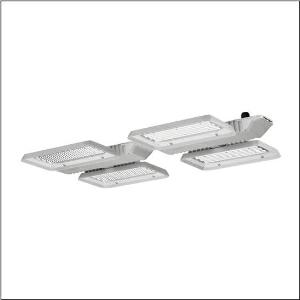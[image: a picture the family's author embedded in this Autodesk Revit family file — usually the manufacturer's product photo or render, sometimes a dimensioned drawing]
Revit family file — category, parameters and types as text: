
# Revit family: highbay_11_51hla2d24nca
name_source: partatom
category: Lighting Fixtures
units: mm (PartAtom-declared; Revit-internal decimal feet)

## family parameters
Cut with Voids When Loaded = No
Host = Face
Light Source = No
Part Type = Normal
Room Calculation Point = No
Round Connector Dimension = Use Diameter
Shared = No

## types (1)
- --- (1 x LED, 33150 lm, 189.6 W, 4000K)
    Apparent Load = 190 VA
    CIE Flux Codes = 89 96 99 100 100
    Color Rendering = 80
    Color Temperature = 4000K
    Default Elevation = 1800 mm
    Description = Highbay 11, LED high bay luminaire, primary light control with lens, of PMMA, light emission: direct distribution, primary light characteristic: symmetric, installation type: surface-mounted, suspended mounting, for 2x 2x LED, rated luminous flux: 33.150lm, luminous efficacy: 175lm/W, light colour: 840, colour temperature: 4000K, control gear: ECG DALI, with terminal, 5-pole, max. 2.5mm², mains connection: 230..240V, AC, 50/60Hz, rated input power: 190W, LED unit, of diecast aluminium, unplated, bead blasted, silver, length: 940mm, width: 500mm, height: 65mm, housing, of diecast aluminium, uncoated, bead blasted, silver, protection rating (complete): IP65, insulation class (complete): insulation class I (protective earthing), certification: CE, ENEC, VDE, UKCA, protection symbol: D, impact resistance: IK08 with glass or PC cover, permissible operating ambient temperature: -35..+45°C, reducing of maximum allowable ambient temperature of 5°C with ceiling mounting, corresponds to IFS (International Featured Standards) requirements for safety and quality in the food industry, packaging unit: 1 piece
    Height = 95 mm
    Lamp = 1 x LED
    Lamp Light Flux = 33150 lm
    Lamp Power = 189.6 W
    Lamp count = 1
    Length = 939 mm
    Luminous efficacy = 175 lm/W
    Manufacturer = Siteco
    ModVariant = No
    Model = 51HLA2D24NCA
    Mounting Place = Ceiling
    Mounting Type = Pendant
    Number of Poles = 1
    OnlyDefault = Yes
    Power Factor = 1
    Product Name = Highbay 11
    Product group = LED high bay luminaire
    ProductGroupID = 903
    Protection Class = Protection class I
    Protection Degree = IP 65
    RLX_Detail_Level = 1
    RLX_Emergency_Light_Flux = 0 lm
    RLX_Emergency_Type = 0
    RLX_Emergency_Type_DB = No
    RlxData = <blob elided: 96629 chars, md5=7aa3dfaa>
    Socket = socket
    Standby Power = 0 W
    System Light Flux = 33150 lm
    System Power = 190 W
    Type Comments = factory setting: luminous flux: 100 % | dim-lin: 254 | 535 mA
    Type Image = l_1003428.jpg
    URL = http://relux.com
    VarID = @adj_145927
    Voltage = 0 V
    Weight = 0.00 kg
    Width = 501 mm

## geometry (parser evidence)
native form markers: Blend x4, Sweep x10
no freeform markers — native parametric forms only
